# Revit family: Bathtub-Free_Standing-American_Standard-Town_Square_S-2544.X02_Series
name_source: partatom
category: Plumbing Fixtures
units: mm (PartAtom-declared; Revit-internal decimal feet)

## family parameters
Always vertical = No
Cut with Voids When Loaded = No
OmniClass Number = 23.45.05.14.21
OmniClass Title = Bathtubs
Part Type = Normal
Room Calculation Point = No
Round Connector Dimension = Use Diameter
Shared = Yes
Work Plane-Based = Yes

## types (4) — shared parameters
ADA Compliant = Yes
Assembly Code = D2010510
CSA B45.5-11 / IAPMO Z124 = Yes
CW Connection = No
CWFU = 3
Default Elevation = 0"
HW Connection = No
HWFU = 3
Height = 20"
Installation Type = Floor Mounted
Length = 32"
Manufacturer = American Standard
Price = Prices may vary. Please consult Manufacturer Representative for most up-to-date price list.
Product Documentation Link = https://americanstandard.box.com
Product Page URL = https://www.americanstandard-us.com
Revised Date = 07/27/2022
Tub Type = Alcove Rectangular Bath Tub
URL = https://www.americanstandard-us.com
Vent Connection = No
WFU = 4
Warranty Information = Limited Lifetime Warranty
Waste Connection = Yes
Waste Connection Diameter = 2 1/8"
Weight (kg) = 74 Lbs. (34 Kg)-502 Lbs.(228 Kg)
Width = 60"
cUPC Compliant = Yes

## per-type parameters (varying)
| type | Bottom Constraint | Description | Finish | Left Drain | Left Offset | Material | Overflow Void Constraint | Right Drain | Right Offset | Waste Location |
| 2544.102.020 | 8 1/8" | Town Square® S 60 x 32-Inch Integral Apron Bathtub With Right-Hand Outlet | Acrylic-American Standard-020-White | No | 3 3/8" | Acrylic-American Standard-020-White | 3 1/2" | Yes | 3 5/16" | 50" |
| 2544.102.222 | 8 1/8" | Town Square® S 60 x 32-Inch Integral Apron Bathtub With Right-Hand Outlet | Acrylic-American Standard-222-Linen | No | 3 3/8" | Acrylic-American Standard-222-Linen | 3 1/2" | Yes | 3 5/16" | 50" |
| 2544.202.020 | 2 5/16" | Town Square® S 60 x 32-Inch Integral Apron Bathtub With Left-Hand Outlet | Acrylic-American Standard-020-White | Yes | 3 5/16" | Acrylic-American Standard-020-White | 49 1/2" | No | 3 3/8" | 10" |
| 2544.202.222 | 2 5/16" | Town Square® S 60 x 32-Inch Integral Apron Bathtub With Right-Hand Outlet | Acrylic-American Standard-222-Linen | Yes | 3 5/16" | Acrylic-American Standard-222-Linen | 49 1/2" | No | 3 3/8" | 10" |

note: column(s) folded — value = type name in every type: Model

## geometry (parser evidence)
native form markers: Sweep x2
no freeform markers — native parametric forms only
